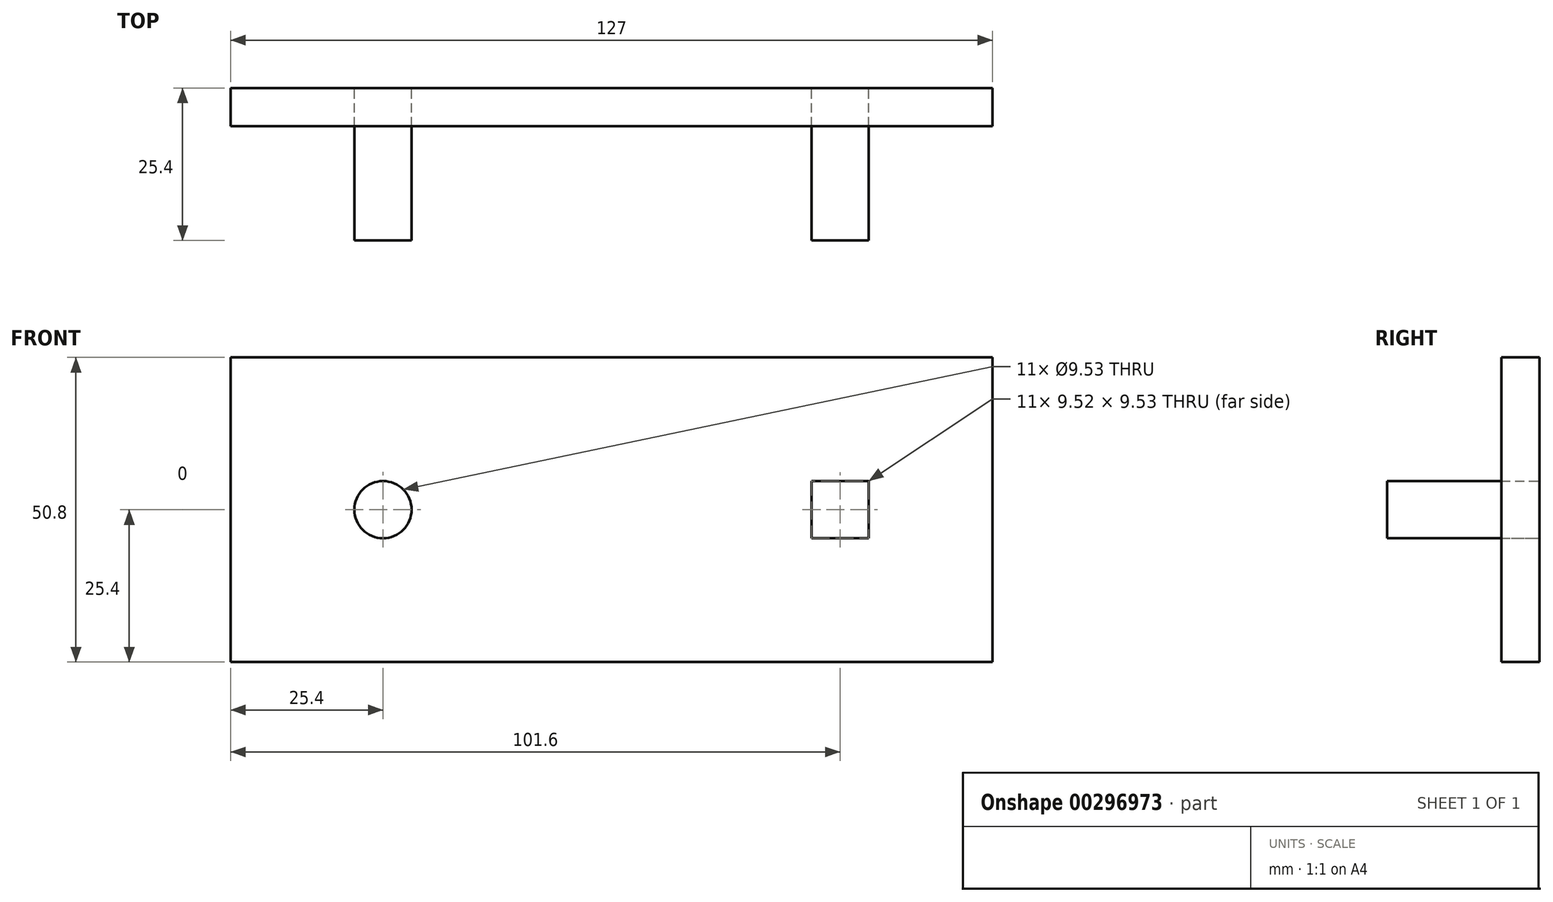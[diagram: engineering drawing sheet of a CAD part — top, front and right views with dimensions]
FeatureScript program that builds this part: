
annotation { "Feature Type Name" : "Feature", "Feature Type Description" : "" }
export const myFeature = defineFeature(function(context is Context, id is Id, definition is map)
    precondition{}
    {
        {
            var Q0;
            Q0=qCreatedBy(makeId("Front.planeOp"),FACE);
            var sketch = newSketch(context, id + "F0", { "sketchPlane" : qUnion([Q0])});
            skLineSegment(sketch, "E0.bottom", {"start": v(-63.5, -25.4) * mm, "end": v(63.5, -25.4) * mm});
            skLineSegment(sketch, "E0.top", {"start": v(-63.5, 25.4) * mm, "end": v(63.5, 25.4) * mm});
            skLineSegment(sketch, "E0.left", {"start": v(-63.5, -25.4) * mm, "end": v(-63.5, 25.4) * mm});
            skLineSegment(sketch, "E0.right", {"start": v(63.5, -25.4) * mm, "end": v(63.5, 25.4) * mm});
            skPoint(sketch, "E0.middle", {"position": v(0, 0) * mm});
            skLineSegment(sketch, "E1.bottom", {"start": v(42.86, -4.76) * mm, "end": v(33.34, -4.76) * mm});
            skLineSegment(sketch, "E1.top", {"start": v(42.86, 4.76) * mm, "end": v(33.34, 4.76) * mm});
            skLineSegment(sketch, "E1.left", {"start": v(42.86, -4.76) * mm, "end": v(42.86, 4.76) * mm});
            skLineSegment(sketch, "E1.right", {"start": v(33.34, -4.76) * mm, "end": v(33.34, 4.76) * mm});
            skPoint(sketch, "E1.middle", {"position": v(38.1, 0) * mm});
            skCircle(sketch, "E2", {"center": v(-38.1, 0) * mm, "radius": 4.76 * mm});
            skSolve(sketch);
        }
        {
            var Q0;
            Q0=makeQuery(id+"F0.imprint","IMPRINT",FACE,{"disambiguationData":[TD([[makeQuery(id+"F0.imprint","IMPRINT",EDGE,{"derivedFrom":sQuery(id+"F0.wireOp",EDGE,"E0.bottom")}),1.0]])]});
            extrude(context, id + "F1", {"entities" : qUnion([Q0]), "depth" : 6.35 * mm});
        }
        {
            var Q0;
            Q0=makeQuery(id+"F0.imprint","IMPRINT",FACE,{"disambiguationData":[TD([[makeQuery(id+"F0.imprint","IMPRINT",EDGE,{"derivedFrom":sQuery(id+"F0.wireOp",EDGE,"E1.bottom")}),-1.0]])]});
            var Q1;
            Q1=makeQuery(id+"F0.imprint","IMPRINT",FACE,{"disambiguationData":[TD([[makeQuery(id+"F0.imprint","IMPRINT",EDGE,{"derivedFrom":sQuery(id+"F0.wireOp",EDGE,"E2")}),1.0]])]});
            extrude(context, id + "F2", {"entities" : qUnion([Q0, Q1]), "depth" : 25.4 * mm});
        }
    });
